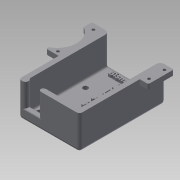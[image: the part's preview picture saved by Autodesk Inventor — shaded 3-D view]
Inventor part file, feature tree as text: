
AUTODESK INVENTOR PART (.ipt)
format: ipt  version: 2015 SP1 (Build 190203100, 203)  size: 1,154,048 bytes
history: native  units: mm
features: extrude x23, sketch x23, projected_geometry x15, fillet x10, reference x2
ambient origin geometry x8: Origin, YZ Plane, XZ Plane, XY Plane, X Axis, Y Axis, Z Axis, Center Point
bodies: Solid1 (feature_tree)
feature tree (73):
  extrude  "Extrusion1"  Depth=60.0mm
  extrude  "Extrusion3"  Depth=3.5mm TaperAngle=0.0deg
  extrude  "Extrusion4"  Depth=3.5mm TaperAngle=0.0deg
  extrude  "Extrusion5"  Depth=3.5mm TaperAngle=0.0deg
  extrude  "Extrusion6"  Depth=6.0mm
  extrude  "Extrusion7"  Depth=2.0mm
  extrude  "Extrusion8"  Depth=2.0mm
  fillet  "Fillet1"  Radius=2.0mm
  extrude  "Extrusion9"  Depth=3.5mm TaperAngle=0.0deg
  extrude  "Extrusion10"  Depth=3.5mm TaperAngle=0.0deg
  fillet  "Fillet2"  Radius=3.5mm
  extrude  "Extrusion11"  Depth=3.5mm TaperAngle=0.0deg
  extrude  "Extrusion12"  Depth=3.5mm TaperAngle=0.0deg
  extrude  "Extrusion13"  Depth=3.5mm
  extrude  "Extrusion14"  Depth=3.5mm
  sketch  "Sketch19"  dims[d76=3.5mm d77=3.5mm]
  fillet  "Fillet3"  Radius=3.5mm
  extrude  "Extrusion16"  Depth=3.5mm
  extrude  "Extrusion17"  Depth=12.5mm
  extrude  "Extrusion18"  Depth=3.5mm TaperAngle=0.0deg
  extrude  "Extrusion19"  Depth=3.5mm TaperAngle=0.0deg
  fillet  "Fillet5"  Radius=2.0mm
  fillet  "Fillet6"  Radius=1.0mm
  fillet  "Fillet7"  Radius=2.0mm
  fillet  "Fillet8"  Radius=1.0mm
  fillet  "Fillet9"  Radius=1.0mm
  fillet  "Fillet10"  Radius=1.0mm
  extrude  "Extrusion20"  Depth=3.5mm TaperAngle=0.0deg
  extrude  "Extrusion21"  Depth=3.5mm TaperAngle=0.0deg
  extrude  "Extrusion22"  Depth=3.0mm TaperAngle=0.0deg
  extrude  "Extrusion23"  [1 undecoded]
  fillet  "Fillet11"  [1 undecoded]
  extrude  "Extrusion24"  [1 undecoded]
  extrude  "Extrusion25"  [1 undecoded]
  sketch  "Sketch1"  dims[d0=42.5mm d1=60.0mm]
  sketch  "Sketch4"  dims[d2=3.5mm d3=0.0mm d11=20.0mm d12=0.0mm]
  sketch  "Sketch5"  dims[d13=3.5mm d14=0.0mm d15=3.5mm d16=0.0mm]
  sketch  "Sketch6"  dims[d17=3.5mm d18=0.0mm d19=3.5mm d20=0.0mm]
  sketch  "Sketch7"  dims[d21=6.0mm d22=6.0mm]
  reference  "Reference1"
  sketch  "Sketch8"  dims[d23=3.5mm d24=2.0mm]
  reference  "Reference2"
  sketch  "Sketch11"  dims[d25=2.0mm d26=2.0mm d27=2.0mm]
  projected_geometry  "Projected Loop1"
  projected_geometry  "Projected Loop2"
  projected_geometry  "Projected Loop3"
  sketch  "Sketch12"  dims[d28=3.5mm d29=3.5mm d30=0.0mm]
  sketch  "Sketch13"  dims[d31=2.0mm d32=3.5mm d33=0.0mm d34=3.5mm d35=0.0mm]
  projected_geometry  "Projected Loop4"
  projected_geometry  "Projected Loop5"
  projected_geometry  "Projected Loop6"
  projected_geometry  "Projected Loop7"
  projected_geometry  "Projected Loop8"
  sketch  "Sketch15"  dims[d36=3.0mm d51=3.5mm d52=0.0mm]
  sketch  "Sketch16"  dims[d53=3.5mm d54=0.0mm d55=3.5mm d56=0.0mm]
  sketch  "Sketch17"  dims[d57=3.5mm d58=0.0mm d70=1.25mm]
  sketch  "Sketch18"  dims[d71=11.75mm d72=16.0mm d73=3.5mm d74=0.0mm]
  sketch  "Sketch21"  dims[d78=25.0mm d79=12.5mm]
  projected_geometry  "Projected Loop10"
  sketch  "Sketch22"  dims[d80=20.0mm d81=3.5mm d82=0.0mm]
  projected_geometry  "Projected Loop11"
  sketch  "Sketch23"  dims[d92=3.5mm d93=0.0mm d94=3.5mm d95=0.0mm d96=2.0mm d97=1.0mm d98=2.0mm d99=1.0mm d100=1.0mm d101=1.0mm]
  projected_geometry  "Projected Loop12"
  sketch  "Sketch24"  dims[d102=3.5mm d103=0.0mm d104=3.5mm d105=0.0mm]
  projected_geometry  "Projected Loop13"
  projected_geometry  "Projected Loop14"
  sketch  "Sketch25"  dims[d106=3.5mm d107=0.0mm d108=12.5mm d109=0.0mm]
  sketch  "Sketch26"  dims[d110=1.0mm d111=3.0mm d112=0.0mm]
  projected_geometry  "Projected Loop15"
  sketch  "Sketch27"  dims[d113=2.0mm d114=0.0mm]
  projected_geometry  "Projected Loop16"
  sketch  "Sketch29"
  sketch  "Sketch30"
note: 4 required parameter values undecoded (feature->parameter linkage not recoverable at this tier; creation-order binding heuristic only, values carry confidence <= 0.55)
